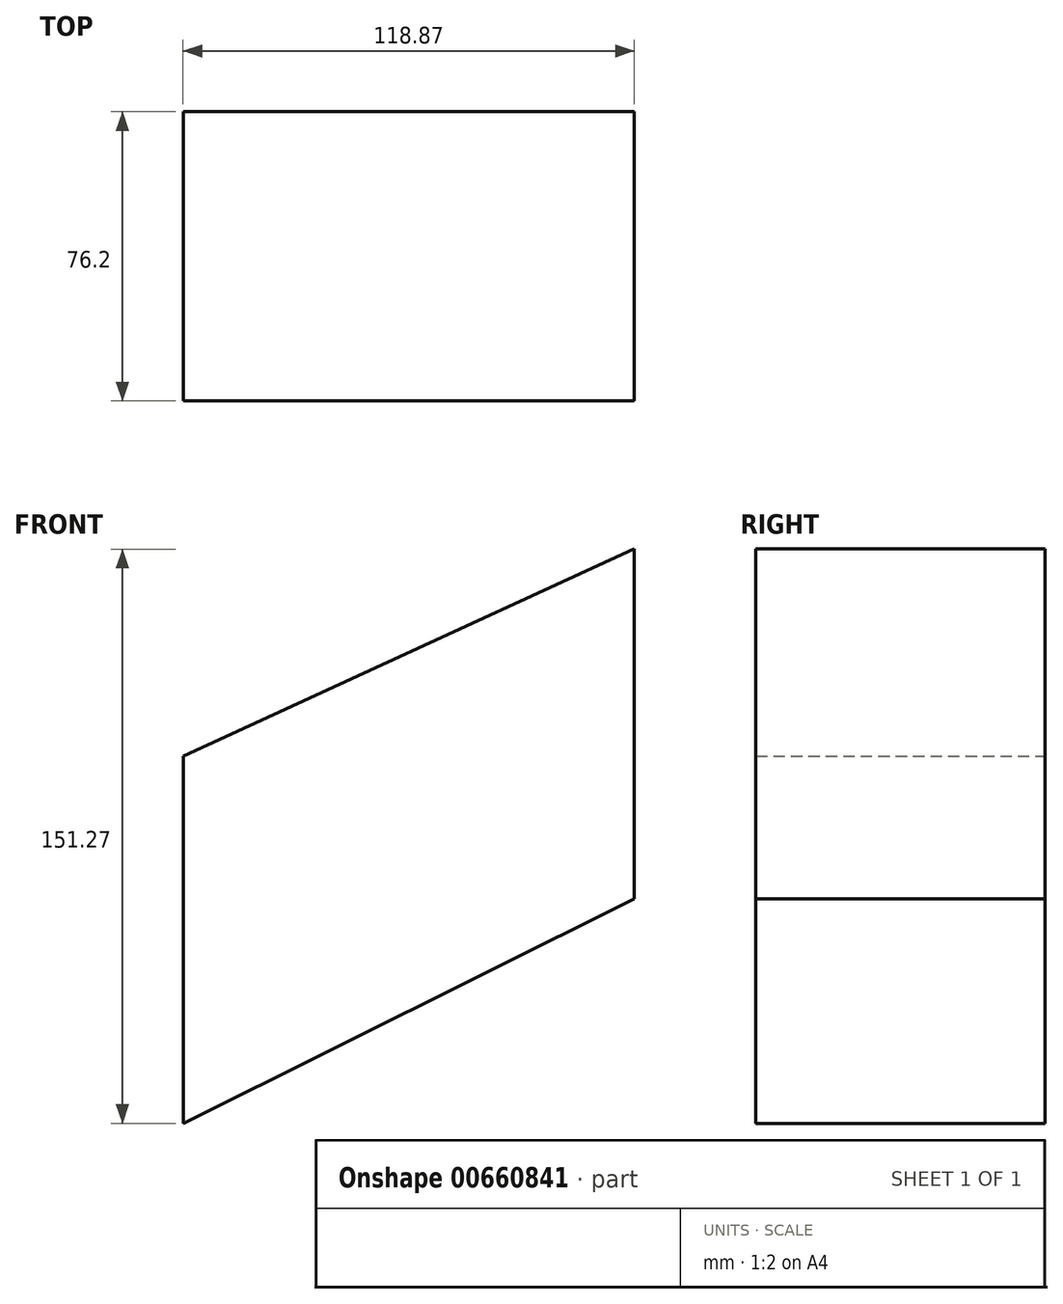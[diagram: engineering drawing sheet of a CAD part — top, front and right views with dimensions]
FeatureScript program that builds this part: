
annotation { "Feature Type Name" : "Feature", "Feature Type Description" : "" }
export const myFeature = defineFeature(function(context is Context, id is Id, definition is map)
    precondition{}
    {
        {
            var Q0;
            Q0=qCreatedBy(makeId("Front.planeOp"),FACE);
            var sketch = newSketch(context, id + "F0", { "sketchPlane" : qUnion([Q0])});
            skLineSegment(sketch, "E0", {"start": v(-68.05, 16.86) * mm, "end": v(-68.05, -79.8) * mm});
            skLineSegment(sketch, "E1", {"start": v(-68.05, 16.86) * mm, "end": v(50.82, 71.46) * mm});
            skLineSegment(sketch, "E2", {"start": v(50.82, 71.46) * mm, "end": v(50.82, -20.7) * mm});
            skLineSegment(sketch, "E3", {"start": v(50.82, -20.7) * mm, "end": v(-68.05, -79.8) * mm});
            skPoint(sketch, "E4.end.orphan", {"position": v(-68.05, -102.68) * mm});
            skSolve(sketch);
        }
        {
            var Q0;
            Q0=makeQuery(id+"F0.imprint","IMPRINT",FACE,{"disambiguationData":[TD([[makeQuery(id+"F0.imprint","IMPRINT",EDGE,{"derivedFrom":sQuery(id+"F0.wireOp",EDGE,"E0")}),1.0]])]});
            extrude(context, id + "F1", {"entities" : qUnion([Q0]), "depth" : 76.2 * mm, "offsetDistance" : 25.4 * mm});
        }
    });
